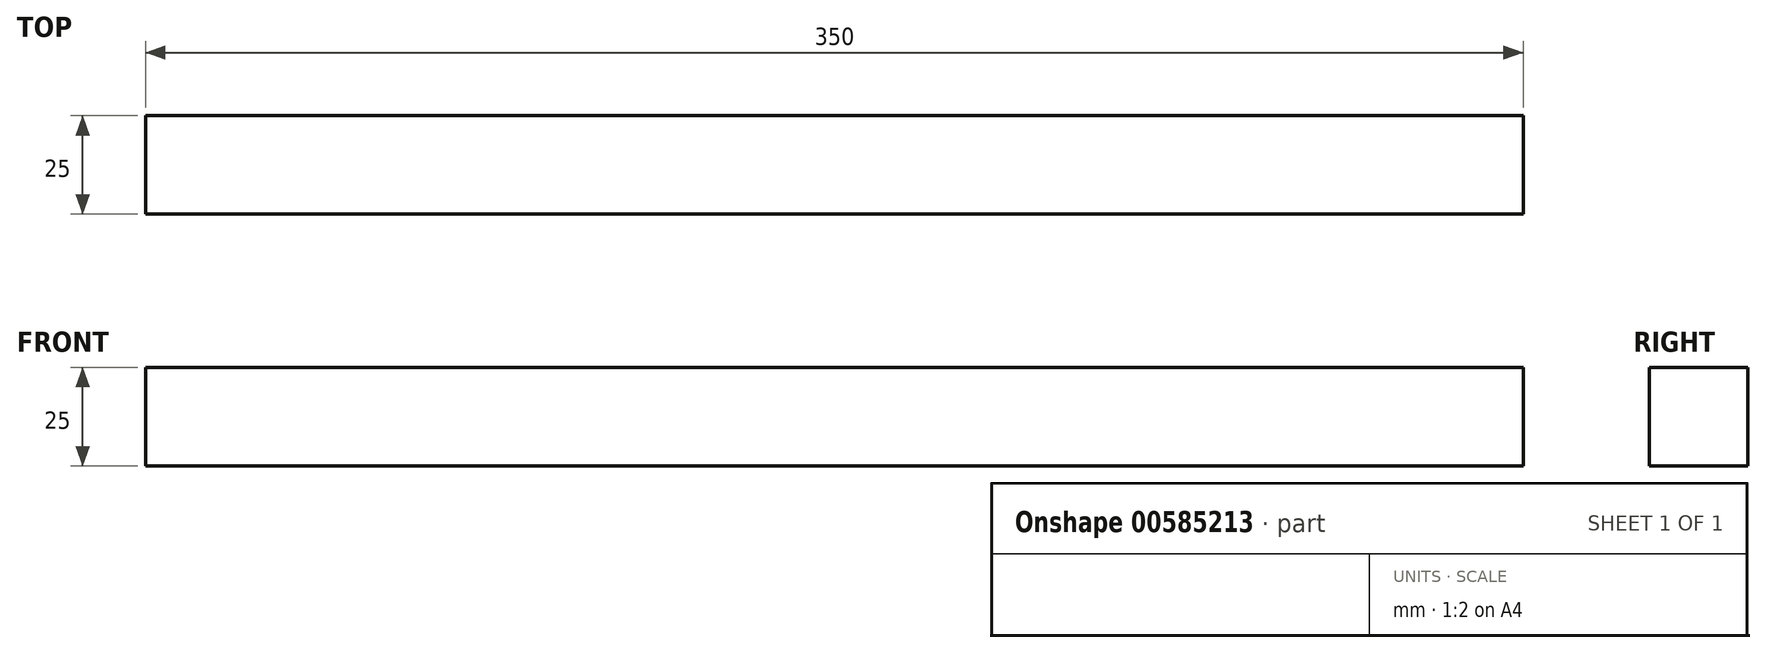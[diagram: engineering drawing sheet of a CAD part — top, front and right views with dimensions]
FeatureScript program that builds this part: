
annotation { "Feature Type Name" : "Feature", "Feature Type Description" : "" }
export const myFeature = defineFeature(function(context is Context, id is Id, definition is map)
    precondition{}
    {
        {
            var Q0;
            Q0=qCreatedBy(makeId("Front.planeOp"),FACE);
            var sketch = newSketch(context, id + "F0", { "sketchPlane" : qUnion([Q0])});
            skLineSegment(sketch, "E0.bottom", {"start": v(0, 0) * mm, "end": v(350, 0) * mm});
            skLineSegment(sketch, "E0.top", {"start": v(0, 25) * mm, "end": v(350, 25) * mm});
            skLineSegment(sketch, "E0.left", {"start": v(0, 0) * mm, "end": v(0, 25) * mm});
            skLineSegment(sketch, "E0.right", {"start": v(350, 0) * mm, "end": v(350, 25) * mm});
            skSolve(sketch);
        }
        {
            var Q0;
            Q0=makeQuery(id+"F0.imprint","IMPRINT",FACE,{"disambiguationData":[TD([[makeQuery(id+"F0.imprint","IMPRINT",EDGE,{"derivedFrom":sQuery(id+"F0.wireOp",EDGE,"E0.bottom")}),1.0]])]});
            extrude(context, id + "F1", {"entities" : qUnion([Q0]), "endBound" : BoundingType.SYMMETRIC, "depth" : 25 * mm, "offsetDistance" : 25 * mm});
        }
    });
